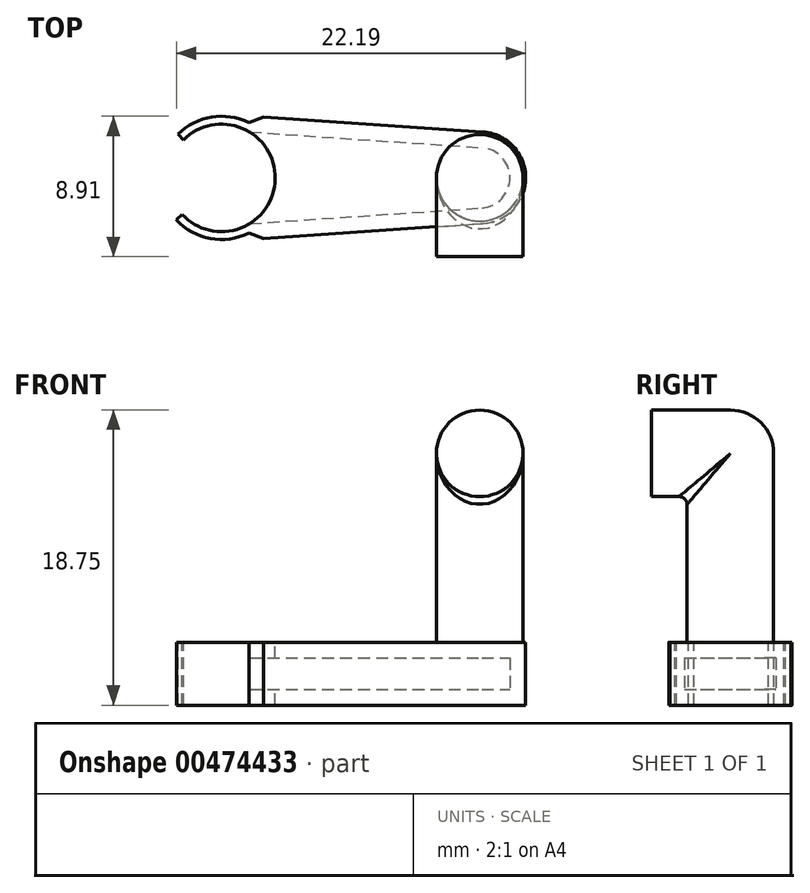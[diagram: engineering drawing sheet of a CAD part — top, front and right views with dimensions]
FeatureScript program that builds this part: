
annotation { "Feature Type Name" : "Feature", "Feature Type Description" : "" }
export const myFeature = defineFeature(function(context is Context, id is Id, definition is map)
    precondition{}
    {
        {
            var Q0;
            Q0=qCreatedBy(makeId("Top.planeOp"),FACE);
            var sketch = newSketch(context, id + "F0", { "sketchPlane" : qUnion([Q0])});
            skArc(sketch, "E0", {"start": v(-2.5, -2.32) * mm, "mid": v(3.41, -0.06) * mm, "end": v(-2.42, 2.41) * mm});
            skArc(sketch, "E1", {"start": v(-2.87, -2.66) * mm, "mid": v(3.91, -0.07) * mm, "end": v(-2.77, 2.76) * mm});
            skLineSegment(sketch, "E2", {"start": v(-2.42, 2.41) * mm, "end": v(-2.77, 2.76) * mm});
            skLineSegment(sketch, "E3", {"start": v(-2.5, -2.32) * mm, "end": v(-2.87, -2.66) * mm});
            skPoint(sketch, "E4", {"position": v(2.68, 2.85) * mm});
            skArc(sketch, "E5", {"start": v(16.53, -1.91) * mm, "mid": v(18.32, 0) * mm, "end": v(16.53, 1.91) * mm});
            skLineSegment(sketch, "E6", {"start": v(2.68, 2.85) * mm, "end": v(16.53, 1.91) * mm});
            skLineSegment(sketch, "E7", {"start": v(2.68, -2.85) * mm, "end": v(16.53, -1.91) * mm});
            skLineSegment(sketch, "E8", {"start": v(2.68, 2.85) * mm, "end": v(2.68, 3.85) * mm});
            skArc(sketch, "E9", {"start": v(16.6, -2.9) * mm, "mid": v(19.32, 0) * mm, "end": v(16.6, 2.9) * mm});
            skLineSegment(sketch, "E10", {"start": v(2.68, 3.85) * mm, "end": v(16.6, 2.9) * mm});
            skLineSegment(sketch, "E11", {"start": v(2.68, -3.85) * mm, "end": v(16.6, -2.9) * mm});
            skLineSegment(sketch, "E12", {"start": v(2.68, -3.85) * mm, "end": v(1.75, -3.5) * mm});
            skLineSegment(sketch, "E13", {"start": v(2.68, 3.85) * mm, "end": v(1.75, 3.5) * mm});
            skLineSegment(sketch, "E14", {"start": v(2.68, -2.85) * mm, "end": v(1.79, -2.91) * mm});
            skLineSegment(sketch, "E15", {"start": v(2.68, 2.85) * mm, "end": v(1.79, 2.91) * mm});
            skSolve(sketch);
        }
        {
            var Q0;
            {var subQ0=sQuery(id+"F0.wireOp",EDGE,"CKcWzJf1-aWjw-Eu1f-9tFN-VUDR9NxraWUW");Q0=makeQuery(id+"F0.imprint","IMPRINT",FACE,{"disambiguationData":[TD([[makeQuery(id+"F0.imprint","IMPRINT",EDGE,{"derivedFrom":subQ0}),-1.0]])]});}
            var Q1;
            {var subQ1=sQuery(id+"F0.wireOp",EDGE,"E5");var subQ6=sQuery(id+"F0.wireOp",EDGE,"E6");var subQ8=makeQuery(id+"F0.imprint","INTERSECT",VERTEX,{"derivedFrom":[subQ1,subQ6]});Q1=makeQuery(id+"F0.imprint","IMPRINT",FACE,{"disambiguationData":[TD([[makeQuery(id+"F0.imprint","IMPRINT",EDGE,{"disambiguationData":[TD([[subQ8,1.0]])],"derivedFrom":subQ1}),-1.0]])]});}
            var Q2;
            {var subQ4=sQuery(id+"F0.wireOp",EDGE,"E0");var subQ6=sQuery(id+"F0.wireOp",EDGE,"E3");var subQ8=makeQuery(id+"F0.imprint","INTERSECT",VERTEX,{"derivedFrom":[subQ4,subQ6]});Q2=makeQuery(id+"F0.imprint","IMPRINT",FACE,{"disambiguationData":[TD([[makeQuery(id+"F0.imprint","IMPRINT",EDGE,{"disambiguationData":[TD([[subQ8,-1.0]])],"derivedFrom":subQ4}),-1.0]])]});}
            var Q3;
            {var subQ0=sQuery(id+"F0.wireOp",EDGE,"E8");Q3=makeQuery(id+"F0.imprint","IMPRINT",FACE,{"disambiguationData":[TD([[makeQuery(id+"F0.imprint","IMPRINT",EDGE,{"derivedFrom":subQ0}),-1.0]])]});}
            var Q4;
            {var subQ0=sQuery(id+"F0.wireOp",EDGE,"E5");var subQ1=sQuery(id+"F0.wireOp",EDGE,"uXQZlskG-9AV4-Go2M-dcmM-tuJ8wE5xBhPz");var subQ2=makeQuery(id+"F0.imprint","INTERSECT",VERTEX,{"derivedFrom":[subQ1,subQ0]});Q4=makeQuery(id+"F0.imprint","IMPRINT",FACE,{"disambiguationData":[TD([[makeQuery(id+"F0.imprint","IMPRINT",EDGE,{"disambiguationData":[TD([[subQ2,1.0]])],"derivedFrom":subQ1}),1.0]])]});}
            var Q5;
            {var subQ0=sQuery(id+"F0.wireOp",EDGE,"CKcWzJf1-aWjw-Eu1f-9tFN-VUDR9NxraWUW");Q5=makeQuery(id+"F0.imprint","IMPRINT",FACE,{"disambiguationData":[TD([[makeQuery(id+"F0.imprint","IMPRINT",EDGE,{"derivedFrom":subQ0}),1.0]])]});}
            var Q6;
            {var subQ0=sQuery(id+"F0.wireOp",EDGE,"toj4CKy1-vWCa-lfUr-aQuA-G30epw7Z8bVJ");var subQ1=sQuery(id+"F0.wireOp",EDGE,"E0");var subQ2=makeQuery(id+"F0.imprint","INTERSECT",VERTEX,{"disambiguationData":[OD(0.0)],"derivedFrom":[subQ1,subQ0]});Q6=makeQuery(id+"F0.imprint","IMPRINT",FACE,{"disambiguationData":[TD([[makeQuery(id+"F0.imprint","IMPRINT",EDGE,{"disambiguationData":[TD([[subQ2,1.0]])],"derivedFrom":subQ1}),-1.0]])]});}
            var Q7;
            {var subQ0=sQuery(id+"F0.wireOp",EDGE,"E5");var subQ1=sQuery(id+"F0.wireOp",EDGE,"uXQZlskG-9AV4-Go2M-dcmM-tuJ8wE5xBhPz");var subQ2=makeQuery(id+"F0.imprint","INTERSECT",VERTEX,{"derivedFrom":[subQ1,subQ0]});Q7=makeQuery(id+"F0.imprint","IMPRINT",FACE,{"disambiguationData":[TD([[makeQuery(id+"F0.imprint","IMPRINT",EDGE,{"disambiguationData":[TD([[subQ2,1.0]])],"derivedFrom":subQ1}),-1.0]])]});}
            var Q8;
            {var subQ4=sQuery(id+"F0.wireOp",EDGE,"E0");var subQ6=sQuery(id+"F0.wireOp",EDGE,"toj4CKy1-vWCa-lfUr-aQuA-G30epw7Z8bVJ");var subQ8=makeQuery(id+"F0.imprint","INTERSECT",VERTEX,{"disambiguationData":[OD(0.0)],"derivedFrom":[subQ4,subQ6]});Q8=makeQuery(id+"F0.imprint","IMPRINT",FACE,{"disambiguationData":[TD([[makeQuery(id+"F0.imprint","IMPRINT",EDGE,{"disambiguationData":[TD([[subQ8,-1.0]])],"derivedFrom":subQ4}),-1.0]])]});}
            var Q9;
            {var subQ0=sQuery(id+"F0.wireOp",EDGE,"uXQZlskG-9AV4-Go2M-dcmM-tuJ8wE5xBhPz");var subQ1=sQuery(id+"F0.wireOp",EDGE,"E0");var subQ2=makeQuery(id+"F0.imprint","INTERSECT",VERTEX,{"derivedFrom":[subQ1,subQ0]});Q9=makeQuery(id+"F0.imprint","IMPRINT",FACE,{"disambiguationData":[TD([[makeQuery(id+"F0.imprint","IMPRINT",EDGE,{"disambiguationData":[TD([[subQ2,1.0]])],"derivedFrom":subQ1}),-1.0]])]});}
            var Q10;
            {var subQ0=sQuery(id+"F0.wireOp",EDGE,"E5");var subQ1=makeQuery(id+"F0.imprint","INTERSECT",VERTEX,{"derivedFrom":[subQ0,sQuery(id+"F0.wireOp",EDGE,"E6")]});Q10=makeQuery(id+"F0.imprint","IMPRINT",FACE,{"disambiguationData":[TD([[makeQuery(id+"F0.imprint","IMPRINT",EDGE,{"disambiguationData":[TD([[subQ1,-1.0]])],"derivedFrom":subQ0}),1.0]])]});}
            var Q11;
            {var subQ0=sQuery(id+"F0.wireOp",EDGE,"E8");Q11=makeQuery(id+"F0.imprint","IMPRINT",FACE,{"disambiguationData":[TD([[makeQuery(id+"F0.imprint","IMPRINT",EDGE,{"derivedFrom":subQ0}),1.0]])]});}
            var Q12;
            {var subQ1=sQuery(id+"F0.wireOp",EDGE,"E1");var subQ3=sQuery(id+"F0.wireOp",EDGE,"uXQZlskG-9AV4-Go2M-dcmM-tuJ8wE5xBhPz");var subQ4=makeQuery(id+"F0.imprint","INTERSECT",VERTEX,{"derivedFrom":[subQ1,subQ3]});Q12=makeQuery(id+"F0.imprint","IMPRINT",FACE,{"disambiguationData":[TD([[makeQuery(id+"F0.imprint","IMPRINT",EDGE,{"disambiguationData":[TD([[subQ4,-1.0]])],"derivedFrom":subQ3}),-1.0]])]});}
            var Q13;
            {var subQ1=sQuery(id+"F0.wireOp",EDGE,"E1");var subQ3=sQuery(id+"F0.wireOp",EDGE,"uXQZlskG-9AV4-Go2M-dcmM-tuJ8wE5xBhPz");var subQ4=makeQuery(id+"F0.imprint","INTERSECT",VERTEX,{"derivedFrom":[subQ1,subQ3]});Q13=makeQuery(id+"F0.imprint","IMPRINT",FACE,{"disambiguationData":[TD([[makeQuery(id+"F0.imprint","IMPRINT",EDGE,{"disambiguationData":[TD([[subQ4,-1.0]])],"derivedFrom":subQ3}),1.0]])]});}
            var Q14;
            {var subQ0=sQuery(id+"F0.wireOp",EDGE,"E2");Q14=makeQuery(id+"F0.imprint","IMPRINT",FACE,{"disambiguationData":[TD([[makeQuery(id+"F0.imprint","IMPRINT",EDGE,{"derivedFrom":subQ0}),-1.0]])]});}
            extrude(context, id + "F1", {"entities" : qUnion([Q0, Q1, Q2, Q3, Q4, Q5, Q6, Q7, Q8, Q9, Q10, Q11, Q12, Q13, Q14]), "oppositeDirection" : true, "depth" : 1 * mm});
        }
        {
            var Q0;
            {var subQ0=sQuery(id+"F0.wireOp",EDGE,"E3");Q0=makeQuery(id+"F0.imprint","IMPRINT",FACE,{"disambiguationData":[TD([[makeQuery(id+"F0.imprint","IMPRINT",EDGE,{"derivedFrom":subQ0}),1.0]])]});}
            var Q1;
            {var subQ0=sQuery(id+"F0.wireOp",EDGE,"E14");Q1=makeQuery(id+"F0.imprint","IMPRINT",FACE,{"disambiguationData":[TD([[makeQuery(id+"F0.imprint","IMPRINT",EDGE,{"derivedFrom":subQ0}),-1.0]])]});}
            var Q2;
            {var subQ0=sQuery(id+"F0.wireOp",EDGE,"E2");Q2=makeQuery(id+"F0.imprint","IMPRINT",FACE,{"disambiguationData":[TD([[makeQuery(id+"F0.imprint","IMPRINT",EDGE,{"derivedFrom":subQ0}),-1.0]])]});}
            var Q3;
            {var subQ0=sQuery(id+"F0.wireOp",EDGE,"E8");Q3=makeQuery(id+"F0.imprint","IMPRINT",FACE,{"disambiguationData":[TD([[makeQuery(id+"F0.imprint","IMPRINT",EDGE,{"derivedFrom":subQ0}),1.0]])]});}
            var Q4;
            Q4=makeQuery(id+"F0.imprint","IMPRINT",FACE,{"disambiguationData":[TD([[makeQuery(id+"F0.imprint","IMPRINT",EDGE,{"derivedFrom":sQuery(id+"F0.wireOp",EDGE,"E5")}),-1.0]])]});
            var Q5;
            Q5=makeQuery(id+"F0.imprint","IMPRINT",FACE,{"disambiguationData":[TD([[makeQuery(id+"F0.imprint","IMPRINT",EDGE,{"derivedFrom":sQuery(id+"F0.wireOp",EDGE,"E5")}),1.0]])]});
            extrude(context, id + "F2", {"entities" : qUnion([Q0, Q1, Q2, Q3, Q4, Q5]), "operationType" : NewBodyOperationType.ADD, "depth" : 3 * mm});
        }
        {
            var Q0;
            Q0=makeQuery(id+"F0.imprint","IMPRINT",FACE,{"disambiguationData":[TD([[makeQuery(id+"F0.imprint","IMPRINT",EDGE,{"derivedFrom":sQuery(id+"F0.wireOp",EDGE,"E5")}),1.0]])]});
            var Q1;
            {var subQ0=sQuery(id+"F0.wireOp",EDGE,"E14");Q1=makeQuery(id+"F0.imprint","IMPRINT",FACE,{"disambiguationData":[TD([[makeQuery(id+"F0.imprint","IMPRINT",EDGE,{"derivedFrom":subQ0}),-1.0]])]});}
            extrude(context, id + "F3", {"entities" : qUnion([Q0, Q1]), "operationType" : NewBodyOperationType.REMOVE, "depth" : 2 * mm});
        }
        {
            var Q0;
            Q0=makeQuery(id+"F2.opExtrude","CAP_FACE",FACE,{"disambiguationData":[OSD([sQuery(id+"F0.wireOp",EDGE,"E0"),sQuery(id+"F0.wireOp",EDGE,"E1"),sQuery(id+"F0.wireOp",EDGE,"E2"),sQuery(id+"F0.wireOp",EDGE,"E3"),sQuery(id+"F0.wireOp",EDGE,"E9"),sQuery(id+"F0.wireOp",EDGE,"E10"),sQuery(id+"F0.wireOp",EDGE,"E11"),sQuery(id+"F0.wireOp",EDGE,"E12"),sQuery(id+"F0.wireOp",EDGE,"E13")])],"isStart":false});
            var sketch = newSketch(context, id + "F4", { "sketchPlane" : qUnion([Q0])});
            skCircle(sketch, "E16", {"center": v(16.4, 0) * mm, "radius": 2.75 * mm});
            skSolve(sketch);
        }
        {
            var Q0;
            Q0 = qSketchRegion(id + "F4", true);
            extrude(context, id + "F5", {"entities" : qUnion([Q0]), "operationType" : NewBodyOperationType.ADD, "depth" : 12 * mm});
        }
        {
            var Q0;
            Q0=makeQuery(id+"F5.opExtrude","CAP_FACE",FACE,{"disambiguationData":[OSD([sQuery(id+"F4.wireOp",EDGE,"E16")])],"isStart":false});
            var sketch = newSketch(context, id + "F6", { "sketchPlane" : qUnion([Q0])});
            skCircle(sketch, "E17", {"center": v(16.4, 0) * mm, "radius": 2.75 * mm});
            skLineSegment(sketch, "E18", {"start": v(13.65, 0) * mm, "end": v(19.15, 0) * mm});
            skSolve(sketch);
        }
        {
            var Q0;
            {var subQ0=sQuery(id+"F6.wireOp",EDGE,"E18");Q0=makeQuery(id+"F6.imprint","IMPRINT",FACE,{"disambiguationData":[TD([[makeQuery(id+"F6.imprint","IMPRINT",EDGE,{"derivedFrom":subQ0}),1.0]])]});}
            var Q1;
            Q1=sQuery(id+"F6.wireOp",EDGE,"E18");
            revolve(context, id + "F7", {"operationType" : NewBodyOperationType.ADD, "entities" : qUnion([Q0]), "axis" : qUnion([Q1]), "revolveType" : RevolveType.ONE_DIRECTION, "angle" : 90 * degree});
        }
        {
            var Q0;
            Q0=makeQuery(id+"F7.opRevolve","CAP_FACE",FACE,{"disambiguationData":[OSD([sQuery(id+"F6.wireOp",EDGE,"E17"),sQuery(id+"F6.wireOp",EDGE,"E18")])],"isStart":false});
            var sketch = newSketch(context, id + "F8", { "sketchPlane" : qUnion([Q0])});
            skCircle(sketch, "E19", {"center": v(16.4, 15) * mm, "radius": 2.75 * mm});
            skSolve(sketch);
        }
        {
            var Q0;
            Q0 = qSketchRegion(id + "F8", true);
            extrude(context, id + "F9", {"entities" : qUnion([Q0]), "operationType" : NewBodyOperationType.ADD, "depth" : 5 * mm});
        }
        {
            var Q0;
            Q0=makeQuery(id+"F9.boolean.opBoolean","INTERSECT",EDGE,{"derivedFrom":[makeQuery(id+"F5.opExtrude","SWEPT_FACE",FACE,{"disambiguationData":[OSD([sQuery(id+"F4.wireOp",EDGE,"E16")])]}),makeQuery(id+"F9.opExtrude","SWEPT_FACE",FACE,{"disambiguationData":[OSD([sQuery(id+"F8.wireOp",EDGE,"E19")])]})]});
            fillet(context, id + "F10", {"entities" : qUnion([Q0]), "radius" : 0.5 * mm, "tangentPropagation" : true, "allowEdgeOverflow" : false});
        }
    });
